# Revit family: IS_Connect_N1384_BIM_DE
name_source: partatom
category: Plumbing Fixtures
revit_build: Autodesk Revit MEP 2016 (Build: 20161004_0715(x64)
units: mm (PartAtom-declared; Revit-internal decimal feet)

## family parameters
Always vertical = No
Cut with Voids When Loaded = No
OmniClass Number = 23.45.05.14.21.11
OmniClass Title = Bath/Shower Units
Part Type = Normal
Room Calculation Point = No
Round Connector Dimension = Use Diameter
Shared = No
Work Plane-Based = No

## types (1)
- N1384AA CONNECT towel ring
    Accessories = www.idealstandard.de\ersatzteile
    AreaUnits = millimeters
    AssetType = Fixed
    BIMObjectName = ISI_IdealStandard_Furniture_Connect_N1384AA
    BIMobject category = Accessories
    BOSUseNativeGeometries = 1
    BarCode = 8014140353690
    Brand = Ideal Standard
    Brand url = http://www.idealstandard.co.uk
    Color = Chrome
    ConnectionType = Mechanical
    CurrencyUnit = €
    Date of publishing = 06/11/2017
    Description = N1384AA CONNECT towel ring
    DurationUnit = year
    EAN code = https://8014140353690
    Edition number = 1
    ExpectedLife = 25
    Features = CONNECT towel ring
    Finish = Chrome
    IFC Classification = Sanitary Terminal
    IfcExportAs = Sanitary Terminal Type
    IfcExportType = TowelRings
    Installation instructions = http://www.idealstandard.de
    InstallationInstructions = www.idealstandard.de\produkte
    LinearUnits = millimeters
    MainColor = Chrome
    MaintenanceInformation = www.idealstandard.de\produkte
    Manufacturer name = Ideal Standard
    ManufacturerURL = www.idealstandard.com
    Model = N1384AA
    ModelNumber = N1384AA
    ModelReference = CONNECT towel ring
    NBS Reference Code = 35-75-91
    NBS Reference Description = Towel Rings
    Name = Furniture_Connect_N1384AA_IdealStandard
    NettWeight = 0,22 kg
    Nominal height = 164
    Nominal width = 160
    NominalDepth = 35 mm  [stored 0.114829 ft]
    NominalHeight = 164 mm  [stored 0.538058 ft]
    NominalLength = 35 mm  [stored 0.114829 ft]
    NominalWidth = 160 mm  [stored 0.524934 ft]
    OmniClass Code = 23-31 25 00
    OmniClass Description = Toilet and Bath Specialties
    Product Guid = 417f3d11-c16e-4c8d-b3fe-580b2a335c37
    Product SKU = N1384
    Product data url = https://bimobject.com
    Product family = CONNECT
    Product group = Accessories
    Product name = CONNECT towel ring
    Product url = http://www.idealstandard.de
    ProductInformation = www.idealstandard.de/produkte
    QR code = http://bimobject.com
    Shape = Sculptured
    Size = 160x35x164 mm
    Space = Internal
    SpareParts = www.idealstandard.de/ersatzteile
    Technical description = http://www.idealstandard.de
    URL = www.idealstandard.com
    Uniclass 1.4 Code = L8245
    Uniclass 1.4 Description = Towel rails
    Uniclass 2.0 Code = PR-35-75-91
    Uniclass 2.0 Description = Towel Rings
    Uniclass 2015 Code = Pr_40_20_76_91
    Uniclass 2015 Name = Towel rings
    Uniclass2015Code = Pr_40_20_76_91
    Uniclass2015Title = Towel rings
    Uniclass2015Version = Products v1.1
    Version = 1
    VolumeUnits = Litres
    Weight Net (Kg) = 0.22

note: [stored X ft] marks values corroborated as IEEE doubles in the binary element streams (Revit-internal decimal feet)

## geometry (parser evidence)
native form markers: Blend x4, Sweep x1
no freeform markers — native parametric forms only
